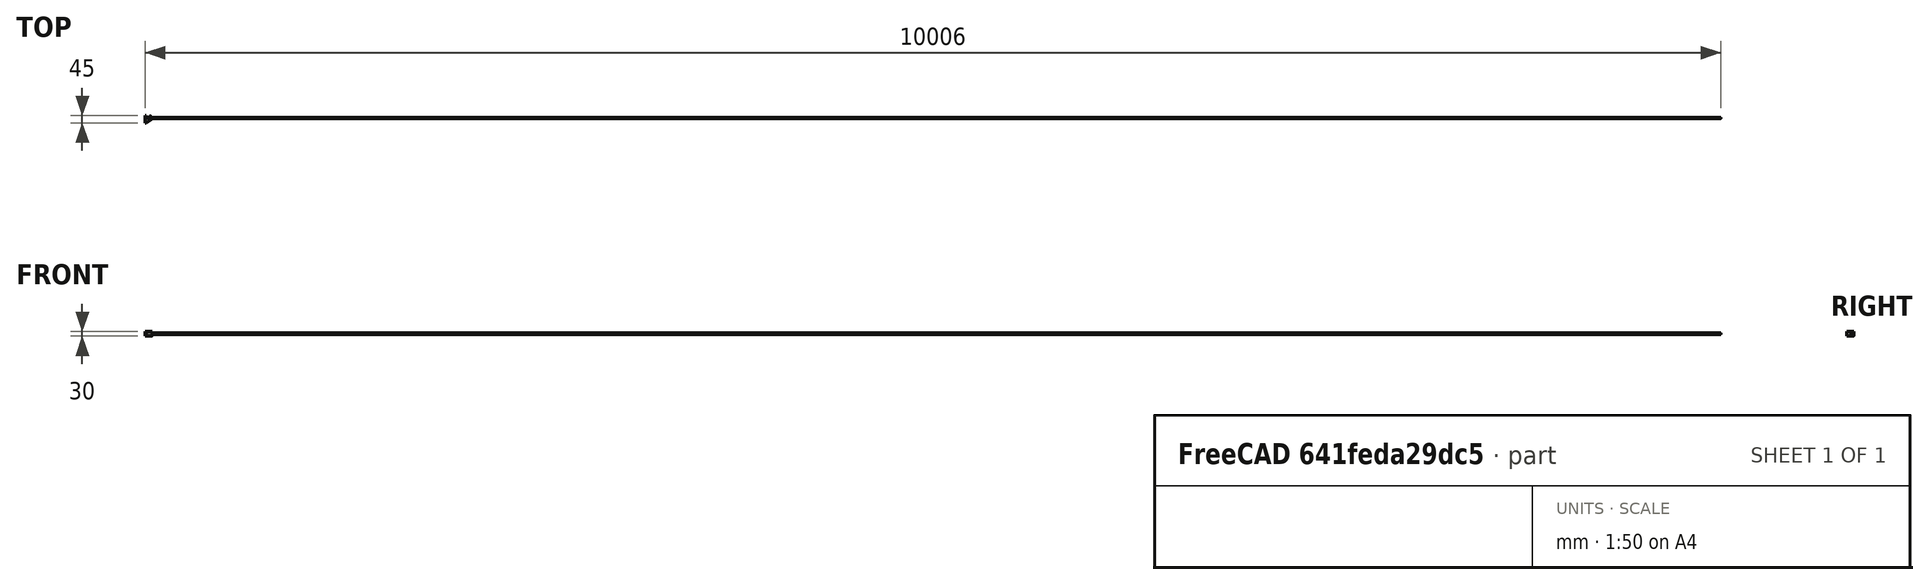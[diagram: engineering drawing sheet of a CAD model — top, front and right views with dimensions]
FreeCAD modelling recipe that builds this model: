
FCSTD DOCUMENT  (FreeCAD 0.16R)
Label: BabyGate3
License: All rights reserved
LicenseURL: http://en.wikipedia.org/wiki/All_rights_reserved
objects: Sketcher::SketchObject×4, PartDesign::Pocket×3, PartDesign::Pad×1, Mesh::Feature×1
note: 12 computed .brp shape members not serialized (recipe doc carries the construction recipe); baked Part::Feature solids carry a one-line shape summary decoded from their .brp

FEATURE [Sketcher::SketchObject] Sketch001
  sketch-geometry (9):
    g0: ArcOfCircle CenterX=0 CenterY=0 CenterZ=0 NormalX=0 NormalY=0 NormalZ=1 Radius=6.35 StartAngle=4.71239 EndAngle=8.01212
    g1: ArcOfCircle CenterX=0 CenterY=0 CenterZ=0 NormalX=0 NormalY=0 NormalZ=1 Radius=12 StartAngle=5.2761 EndAngle=8.01212
    g2: LineSegment StartX=6.41193 StartY=-10.1433 StartZ=0 EndX=-25 EndY=-30 EndZ=0
    g3: LineSegment StartX=0 StartY=-6.35 StartZ=0 EndX=-25 EndY=0 EndZ=0
    g4: LineSegment StartX=-25 StartY=0 StartZ=0 EndX=-25 EndY=15 EndZ=0
    g5: LineSegment StartX=-25 StartY=15 StartZ=0 EndX=-31 EndY=15 EndZ=0
    g6: LineSegment StartX=-31 StartY=15 StartZ=0 EndX=-31 EndY=-30 EndZ=0
    g7: LineSegment StartX=-31 StartY=-30 StartZ=0 EndX=-25 EndY=-30 EndZ=0
    g8: ArcOfCircle CenterX=-1.44488 CenterY=9.06052 CenterZ=0 NormalX=0 NormalY=0 NormalZ=1 Radius=2.825 StartAngle=1.72893 EndAngle=4.87053
  constraints (28):
    c: Coincident(g0,g-1)
    c: PointOnObject(g0,g-2)
    c: Radius(g0) = 6.35
    c: DistanceX(g0,g-1) = 1
    c: Radius(g1) = 12
    c: Coincident(g1,g-1)
    c: Coincident(g2,g1)
    c: DistanceX(g3) = -25
    c: DistanceX(g2) = -25
    c: Coincident(g4,g3)
    c: Vertical(g4)
    c: Coincident(g4,g5)
    c: Coincident(g5,g6)
    c: Vertical(g6)
    c: Coincident(g6,g7)
    c: Horizontal(g5)
    c: Horizontal(g7)
    c: DistanceX(g5,g5) = 6
    c: Tangent(g8,g1)
    c: Coincident(g8,g1)
    c: Coincident(g0,g8)
    c: Coincident(g2,g7)
    c: Tangent(g2,g1)
    c: DistanceY(g5) = 15
    c: DistanceY(g6) = -30
    c: Coincident(g3,g0)
    c: Tangent(g0,g8)
    c: DistanceY(g3) = 0
FEATURE [PartDesign::Pad] Pad
  Length = 30
  Length2 = 100
  Sketch = -> Sketch001
  Type = 0
FEATURE [Sketcher::SketchObject] Sketch002
  Placement = pos=(-31,0,0) rot=(0.57735,-0.57735,-0.57735;2.0944rad)
  Support = -> Pad [Face7]
  sketch-geometry (1):
    g0: Circle CenterX=0 CenterY=15 CenterZ=0 NormalX=0 NormalY=0 NormalZ=1 Radius=2
  constraints (3):
    c: PointOnObject(g0,g-2)
    c: DistanceY(g-1,g0) = 15
    c: Radius(g0) = 2
FEATURE [PartDesign::Pocket] Pocket
  Length = 20
  Sketch = -> Sketch002
  Type = 1
FEATURE [Sketcher::SketchObject] Sketch
  Placement = pos=(-25,0,0) rot=(0.57735,0.57735,0.57735;2.0944rad)
  Support = -> Pocket [Face3]
  sketch-geometry (1):
    g0: Circle CenterX=0 CenterY=15 CenterZ=0 NormalX=0 NormalY=0 NormalZ=1 Radius=3.7
  constraints (3):
    c: Radius(g0) = 3.7
    c: PointOnObject(g0,g-2)
    c: DistanceY(g0) = 15
FEATURE [PartDesign::Pocket] Pocket001
  Length = 5
  Reversed = true
  Sketch = -> Sketch
  Type = 1
FEATURE [Sketcher::SketchObject] Sketch003
  Placement = pos=(-25,0,0) rot=(0.57735,0.57735,0.57735;2.0944rad)
  Support = -> Pocket001 [Face3]
  sketch-geometry (1):
    g0: Circle CenterX=0 CenterY=15 CenterZ=0 NormalX=0 NormalY=0 NormalZ=1 Radius=6.2
  constraints (3):
    c: Radius(g0) = 6.2
    c: PointOnObject(g0,g-2)
    c: DistanceY(g0) = 15
FEATURE [PartDesign::Pocket] Pocket002
  Length = 7
  Reversed = true
  Sketch = -> Sketch003
  Type = 0
FEATURE [Mesh::Feature] Mesh  label="Pocket002 (Meshed)"
